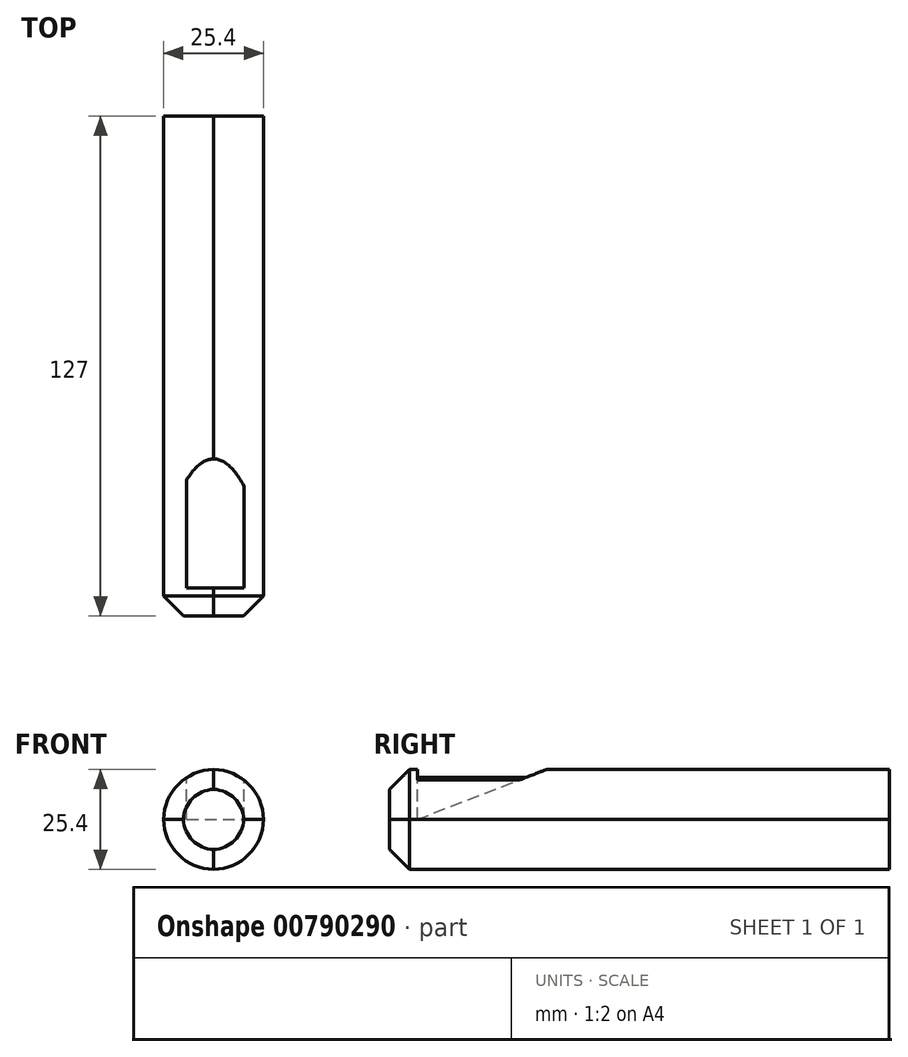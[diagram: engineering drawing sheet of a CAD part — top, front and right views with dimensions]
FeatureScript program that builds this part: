
annotation { "Feature Type Name" : "Feature", "Feature Type Description" : "" }
export const myFeature = defineFeature(function(context is Context, id is Id, definition is map)
    precondition{}
    {
        {
            var Q0;
            Q0=qCreatedBy(makeId("Front.planeOp"),FACE);
            var sketch = newSketch(context, id + "F0", { "sketchPlane" : qUnion([Q0])});
            skLineSegment(sketch, "E0.bottom", {"start": v(-59.55, 16.68) * mm, "end": v(-34.15, 16.68) * mm});
            skLineSegment(sketch, "E0.top", {"start": v(-59.55, 42.08) * mm, "end": v(-34.15, 42.08) * mm});
            skLineSegment(sketch, "E0.left", {"start": v(-59.55, 16.68) * mm, "end": v(-59.55, 42.08) * mm});
            skLineSegment(sketch, "E0.right", {"start": v(-34.15, 16.68) * mm, "end": v(-34.15, 42.08) * mm});
            skSolve(sketch);
        }
        {
            var Q0;
            Q0=makeQuery(id+"F0.imprint","IMPRINT",FACE,{"disambiguationData":[TD([[makeQuery(id+"F0.imprint","IMPRINT",EDGE,{"derivedFrom":sQuery(id+"F0.wireOp",EDGE,"E0.bottom")}),1.0]])]});
            extrude(context, id + "F1", {"entities" : qUnion([Q0]), "depth" : 127 * mm, "offsetDistance" : 25.4 * mm});
        }
        {
            var Q0;
            Q0=makeQuery(id+"F1.opExtrude","SWEPT_FACE",FACE,{"disambiguationData":[OSD([sQuery(id+"F0.wireOp",EDGE,"E0.top")])]});
            var sketch = newSketch(context, id + "F2", { "sketchPlane" : qUnion([Q0])});
            skLineSegment(sketch, "E1.bottom", {"start": v(-53.67, -119.94) * mm, "end": v(-39.13, -119.94) * mm});
            skLineSegment(sketch, "E1.top", {"start": v(-53.67, -87.08) * mm, "end": v(-39.13, -87.08) * mm});
            skLineSegment(sketch, "E1.left", {"start": v(-53.67, -119.94) * mm, "end": v(-53.67, -87.08) * mm});
            skLineSegment(sketch, "E1.right", {"start": v(-39.13, -119.94) * mm, "end": v(-39.13, -87.08) * mm});
            skSolve(sketch);
        }
        {
            var Q0;
            Q0=makeQuery(id+"F2.imprint","IMPRINT",FACE,{"disambiguationData":[TD([[makeQuery(id+"F2.imprint","IMPRINT",EDGE,{"derivedFrom":sQuery(id+"F2.wireOp",EDGE,"E1.bottom")}),1.0]])]});
            extrude(context, id + "F3", {"entities" : qUnion([Q0]), "operationType" : NewBodyOperationType.REMOVE, "oppositeDirection" : true, "depth" : 12.7 * mm, "offsetDistance" : 25.4 * mm});
        }
        {
            var Q0;
            Q0=makeQuery(id+"F3.boolean.opBoolean","COPY",FACE,{"derivedFrom":makeQuery(id+"F3.opExtrude","SWEPT_FACE",FACE,{"disambiguationData":[OSD([sQuery(id+"F2.wireOp",EDGE,"E1.left")])]})});
            var sketch = newSketch(context, id + "F4", { "sketchPlane" : qUnion([Q0])});
            skLineSegment(sketch, "E2", {"start": v(-119.94, 29.38) * mm, "end": v(-87.08, 42.08) * mm});
            skSolve(sketch);
        }
        {
            var Q0;
            Q0=makeQuery(id+"F4.imprint","IMPRINT",FACE,{"disambiguationData":[TD([[makeQuery(id+"F4.imprint","IMPRINT",EDGE,{"derivedFrom":sQuery(id+"F4.wireOp",EDGE,"E2")}),-1.0]])]});
            extrude(context, id + "F5", {"entities" : qUnion([Q0]), "operationType" : NewBodyOperationType.ADD, "depth" : 15.24 * mm, "offsetDistance" : 25.4 * mm});
        }
        {
            var Q0;
            Q0=makeQuery(id+"F1.opExtrude","SWEPT_EDGE",EDGE,{"disambiguationData":[OSD([sQuery(id+"F0.wireOp",EDGE,"E0.top"),sQuery(id+"F0.wireOp",EDGE,"E0.left")])]});
            var Q1;
            Q1=makeQuery(id+"F1.opExtrude","SWEPT_EDGE",EDGE,{"disambiguationData":[OSD([sQuery(id+"F0.wireOp",EDGE,"E0.top"),sQuery(id+"F0.wireOp",EDGE,"E0.right")])]});
            var Q2;
            Q2=makeQuery(id+"F1.opExtrude","SWEPT_EDGE",EDGE,{"disambiguationData":[OSD([sQuery(id+"F0.wireOp",EDGE,"E0.bottom"),sQuery(id+"F0.wireOp",EDGE,"E0.right")])]});
            var Q3;
            Q3=makeQuery(id+"F1.opExtrude","SWEPT_EDGE",EDGE,{"disambiguationData":[OSD([sQuery(id+"F0.wireOp",EDGE,"E0.bottom"),sQuery(id+"F0.wireOp",EDGE,"E0.left")])]});
            fillet(context, id + "F6", {"entities" : qUnion([Q0, Q1, Q2, Q3]), "radius" : 12.88 * mm, "tangentPropagation" : true, "allowEdgeOverflow" : false});
        }
        {
            var Q0;
            {var subQ0=sQuery(id+"F0.wireOp",EDGE,"E0.right");var subQ1=sQuery(id+"F0.wireOp",EDGE,"E0.top");Q0=makeQuery(id+"F6.opFillet","BLEND_EDGE",EDGE,{"blendedFrom":[makeQuery(id+"F1.opExtrude","SWEPT_EDGE",EDGE,{"disambiguationData":[OSD([subQ1,subQ0])]}),makeQuery(id+"F1.opExtrude","CAP_FACE",FACE,{"disambiguationData":[OSD([sQuery(id+"F0.wireOp",EDGE,"E0.bottom"),subQ1,sQuery(id+"F0.wireOp",EDGE,"E0.left"),subQ0])],"isStart":false})],"blendedInto":[makeQuery(id+"F1.opExtrude","CAP_FACE",FACE,{"disambiguationData":[OSD([sQuery(id+"F0.wireOp",EDGE,"E0.bottom"),subQ1,sQuery(id+"F0.wireOp",EDGE,"E0.left"),subQ0])],"isStart":false})]});}
            var Q1;
            Q1=makeQuery(id+"F1.opExtrude","CAP_FACE",FACE,{"disambiguationData":[OSD([sQuery(id+"F0.wireOp",EDGE,"E0.bottom"),sQuery(id+"F0.wireOp",EDGE,"E0.top"),sQuery(id+"F0.wireOp",EDGE,"E0.left"),sQuery(id+"F0.wireOp",EDGE,"E0.right")])],"isStart":false});
            chamfer(context, id + "F7", {"entities" : qUnion([Q0, Q1]), "width" : 5.08 * mm, "tangentPropagation" : true});
        }
    });
